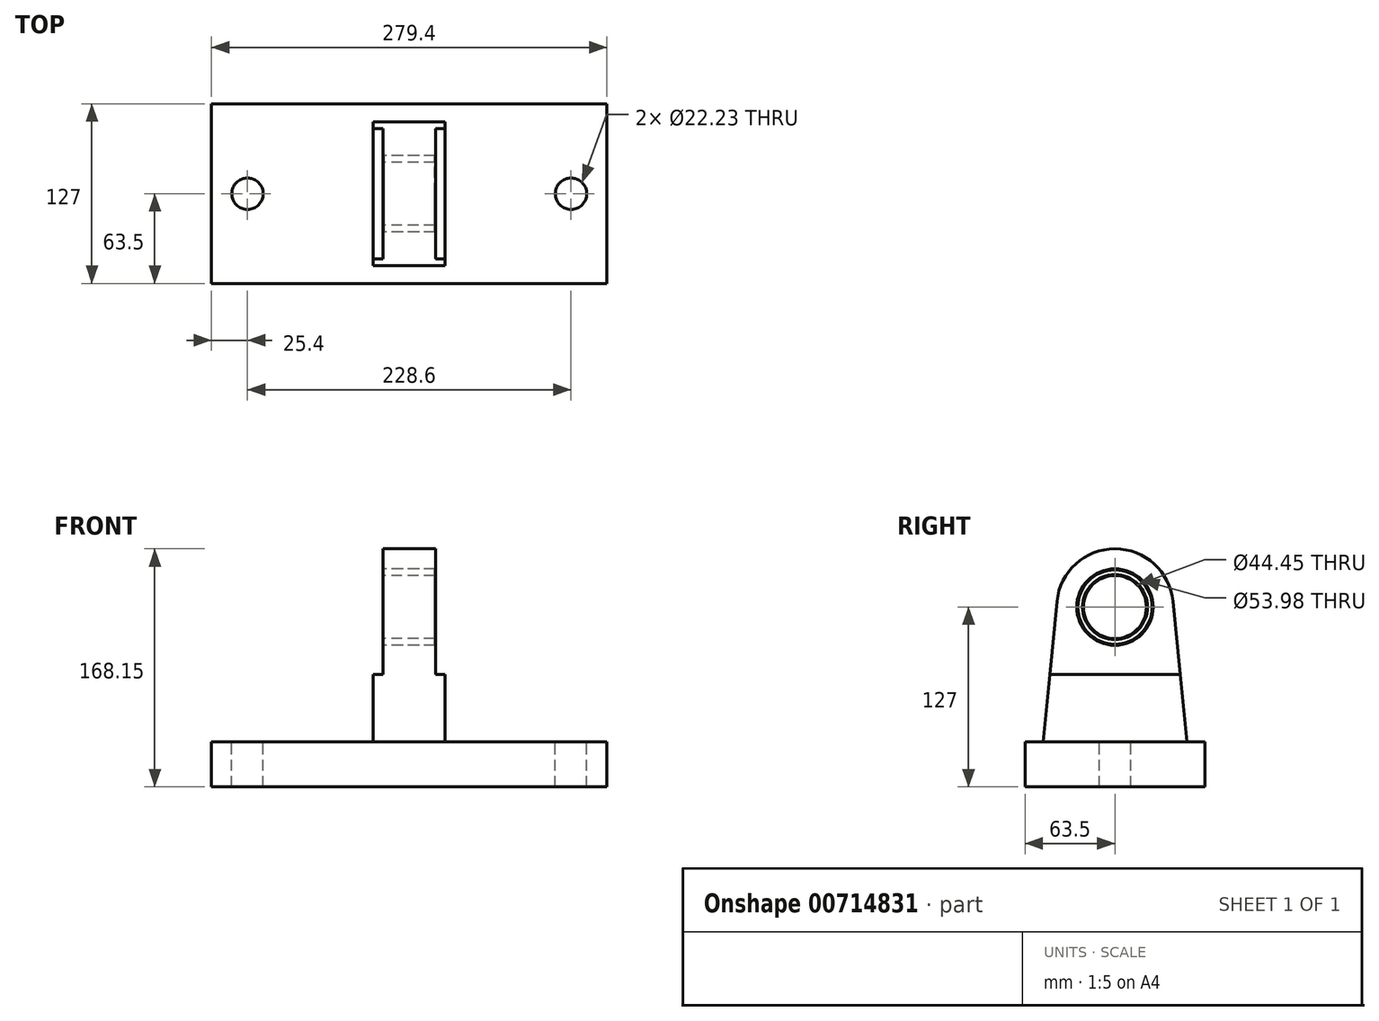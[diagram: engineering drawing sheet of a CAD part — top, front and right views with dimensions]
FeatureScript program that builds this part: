
annotation { "Feature Type Name" : "Feature", "Feature Type Description" : "" }
export const myFeature = defineFeature(function(context is Context, id is Id, definition is map)
    precondition{}
    {
        {
            var Q0;
            Q0=qCreatedBy(makeId("Top.planeOp"),FACE);
            var sketch = newSketch(context, id + "F0", { "sketchPlane" : qUnion([Q0])});
            skLineSegment(sketch, "E0.bottom", {"start": v(-139.7, 63.5) * mm, "end": v(139.7, 63.5) * mm});
            skLineSegment(sketch, "E0.top", {"start": v(-139.7, -63.5) * mm, "end": v(139.7, -63.5) * mm});
            skLineSegment(sketch, "E0.left", {"start": v(-139.7, 63.5) * mm, "end": v(-139.7, -63.5) * mm});
            skLineSegment(sketch, "E0.right", {"start": v(139.7, 63.5) * mm, "end": v(139.7, -63.5) * mm});
            skPoint(sketch, "E0.middle", {"position": v(0, 0) * mm});
            skLineSegment(sketch, "E1", {"start": v(-222.17, 0) * mm, "end": v(218.9, 0) * mm, "construction": true});
            skLineSegment(sketch, "E2", {"start": v(0, 113.93) * mm, "end": v(0, -115.24) * mm, "construction": true});
            skLineSegment(sketch, "E3.0", {"start": v(-114.3, 113.93) * mm, "end": v(-114.3, -115.24) * mm, "construction": true});
            skCircle(sketch, "E4", {"center": v(-114.3, 0) * mm, "radius": 11.11 * mm});
            skCircle(sketch, "E5.MirrorC", {"center": v(114.3, 0) * mm, "radius": 11.11 * mm});
            skSolve(sketch);
        }
        {
            var Q0;
            Q0=makeQuery(id+"F0.imprint","IMPRINT",FACE,{"disambiguationData":[TD([[makeQuery(id+"F0.imprint","IMPRINT",EDGE,{"derivedFrom":sQuery(id+"F0.wireOp",EDGE,"E0.bottom")}),-1.0]])]});
            extrude(context, id + "F1", {"entities" : qUnion([Q0]), "oppositeDirection" : true, "depth" : 31.75 * mm, "offsetDistance" : 25.4 * mm});
        }
        {
            var Q0;
            Q0=qCreatedBy(makeId("Right.planeOp"),FACE);
            var sketch = newSketch(context, id + "F2", { "sketchPlane" : qUnion([Q0])});
            skLineSegment(sketch, "E6", {"start": v(0, 0) * mm, "end": v(0, 95.25) * mm, "construction": true});
            skCircle(sketch, "E7", {"center": v(0, 95.25) * mm, "radius": 26.99 * mm});
            skArc(sketch, "E8", {"start": v(40.95, 99.31) * mm, "mid": v(0, 136.4) * mm, "end": v(-40.95, 99.31) * mm});
            skLineSegment(sketch, "E9.0", {"start": v(50.8, 0) * mm, "end": v(50.8, 95.25) * mm, "construction": true});
            skLineSegment(sketch, "E10", {"start": v(50.8, 0) * mm, "end": v(40.95, 99.31) * mm});
            skLineSegment(sketch, "E11.MirrorCS", {"start": v(-50.8, 0) * mm, "end": v(-40.95, 99.31) * mm});
            skLineSegment(sketch, "E12", {"start": v(50.8, 0) * mm, "end": v(-50.8, 0) * mm});
            skSolve(sketch);
        }
        {
            var Q0;
            Q0 = qSketchRegion(id + "F2", true);
            extrude(context, id + "F3", {"entities" : qUnion([Q0]), "operationType" : NewBodyOperationType.ADD, "endBound" : BoundingType.SYMMETRIC, "depth" : 37.34 * mm, "offsetDistance" : 25.4 * mm});
        }
        {
            var Q0;
            Q0=qCreatedBy(makeId("Right.planeOp"),FACE);
            var sketch = newSketch(context, id + "F4", { "sketchPlane" : qUnion([Q0])});
            skLineSegment(sketch, "E13.0", {"start": v(50.8, 0) * mm, "end": v(-50.8, 0) * mm});
            skLineSegment(sketch, "E14.0", {"start": v(50.8, 0) * mm, "end": v(40.95, 99.31) * mm});
            skLineSegment(sketch, "E15.0", {"start": v(-50.8, 0) * mm, "end": v(-40.95, 99.31) * mm});
            skLineSegment(sketch, "E16.0", {"start": v(50.8, 47.75) * mm, "end": v(-50.8, 47.75) * mm});
            skSolve(sketch);
        }
        {
            var Q0;
            Q0 = qSketchRegion(id + "F4", true);
            extrude(context, id + "F5", {"entities" : qUnion([Q0]), "operationType" : NewBodyOperationType.ADD, "endBound" : BoundingType.SYMMETRIC, "depth" : 50.8 * mm, "offsetDistance" : 25.4 * mm});
        }
        {
            var Q0;
            Q0=qCreatedBy(makeId("Right.planeOp"),FACE);
            var sketch = newSketch(context, id + "F6", { "sketchPlane" : qUnion([Q0])});
            skCircle(sketch, "E17.0", {"center": v(0, 95.25) * mm, "radius": 26.99 * mm});
            skCircle(sketch, "E18", {"center": v(0, 95.25) * mm, "radius": 22.23 * mm});
            skSolve(sketch);
        }
        {
            var Q0;
            Q0 = qSketchRegion(id + "F6", true);
            extrude(context, id + "F7", {"entities" : qUnion([Q0]), "endBound" : BoundingType.SYMMETRIC, "depth" : 37.34 * mm, "offsetDistance" : 25.4 * mm});
        }
        {
            var Q0;
            Q0=makeQuery(id+"F7.opExtrude","CAP_FACE",FACE,{"disambiguationData":[OSD([sQuery(id+"F6.wireOp",EDGE,"E17.0"),sQuery(id+"F6.wireOp",EDGE,"E18")])],"isStart":true});
            var Q1;
            Q1=makeQuery(id+"F7.opExtrude","CAP_FACE",FACE,{"disambiguationData":[OSD([sQuery(id+"F6.wireOp",EDGE,"E17.0"),sQuery(id+"F6.wireOp",EDGE,"E18")])],"isStart":false});
            chamfer(context, id + "F8", {"entities" : qUnion([Q0, Q1]), "width" : 0.76 * mm, "tangentPropagation" : true});
        }
    });
